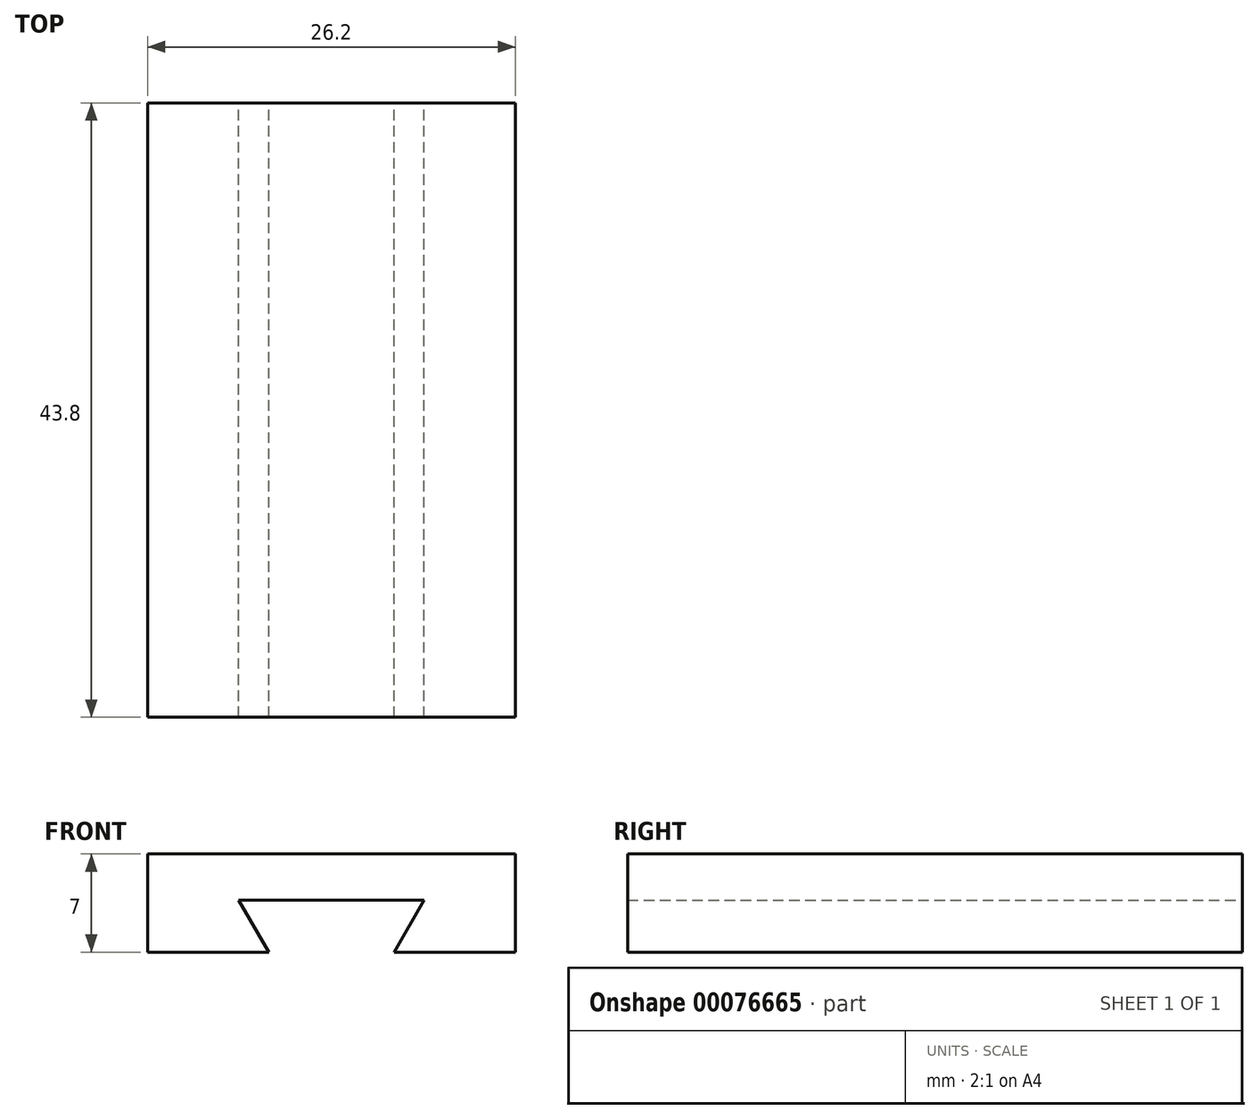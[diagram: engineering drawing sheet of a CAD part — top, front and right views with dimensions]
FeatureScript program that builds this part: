
annotation { "Feature Type Name" : "Feature", "Feature Type Description" : "" }
export const myFeature = defineFeature(function(context is Context, id is Id, definition is map)
    precondition{}
    {
        {
            var Q0;
            Q0=qCreatedBy(makeId("Front.planeOp"),FACE);
            var sketch = newSketch(context, id + "F0", { "sketchPlane" : qUnion([Q0])});
            skLineSegment(sketch, "E0", {"start": v(0, 0) * mm, "end": v(8.64, 0) * mm});
            skLineSegment(sketch, "E1", {"start": v(8.64, 0) * mm, "end": v(6.5, 3.7) * mm});
            skLineSegment(sketch, "E2", {"start": v(6.5, 3.7) * mm, "end": v(19.7, 3.7) * mm});
            skLineSegment(sketch, "E3", {"start": v(19.7, 3.7) * mm, "end": v(17.56, 0) * mm});
            skLineSegment(sketch, "E4", {"start": v(17.56, 0) * mm, "end": v(26.2, 0) * mm});
            skLineSegment(sketch, "E5", {"start": v(26.2, 0) * mm, "end": v(26.2, 7) * mm});
            skLineSegment(sketch, "E6", {"start": v(26.2, 7) * mm, "end": v(0, 7) * mm});
            skLineSegment(sketch, "E7", {"start": v(0, 7) * mm, "end": v(0, 0) * mm});
            skSolve(sketch);
        }
        {
            var Q0;
            Q0 = qSketchRegion(id + "F0", true);
            extrude(context, id + "F1", {"entities" : qUnion([Q0]), "depth" : 43.8 * mm});
        }
    });
